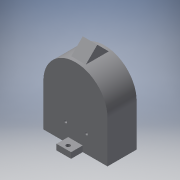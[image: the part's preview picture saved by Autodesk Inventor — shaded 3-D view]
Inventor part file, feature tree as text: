
AUTODESK INVENTOR PART (.ipt)
format: ipt  version: 2016 (Build 200138000, 138)  size: 161,280 bytes
history: native  units: in
note: dims shown in document units (in); Inventor stores cm internally (conversion verified against a paired STEP export)
features: extrude x7, sketch x6, reference x4, plane x1
ambient origin geometry x8: Origin, YZ Plane, XZ Plane, XY Plane, X Axis, Y Axis, Z Axis, Center Point
bodies: Solid1 (feature_tree)
feature tree (18):
  extrude  "Extrusion1"  Depth=0.4in TaperAngle=0.0deg
  extrude  "Extrusion2"  Depth=0.5in
  extrude  "Extrusion4"  Depth=0.4in TaperAngle=0.0deg
  extrude  "Extrusion5"  Depth=0.1378in
  extrude  "Extrusion6"  Depth=0.25in
  plane  "Work Plane1"
  extrude  "Extrusion7"  Depth=0.197in
  extrude  "Extrusion8"  Depth=1.0in
  sketch  "Sketch1"  dims[d1=1.0in d2=0.0in d4=0.4in d5=0.0in]
  reference  "Reference1"
  sketch  "Sketch2"  dims[d10=0.25in d11=0.5in]
  reference  "Reference2"
  sketch  "Sketch5"  dims[d12=0.197in d13=0.4in d14=0.0in]
  sketch  "Sketch6"  dims[d15=0.15in d16=0.1378in]
  sketch  "Sketch7"  dims[d17=0.4in d18=0.0in d19=0.25in]
  sketch  "Sketch8"  dims[d20=0.5in d21=0.197in d22=0.15in d23=0.1772in d24=0.4in d25=0.0in d26=0.25in d27=2.2in d28=-1.1in d29=0.1065in d30=0.787in d31=0.394in d32=0.394in d33=0.5in d34=0.0in d35=0.0394in d36=0.0394in d37=0.098in d38=0.098in d39=1.0in d40=0.0in]
  reference  "Reference3"
  reference  "Reference4"
